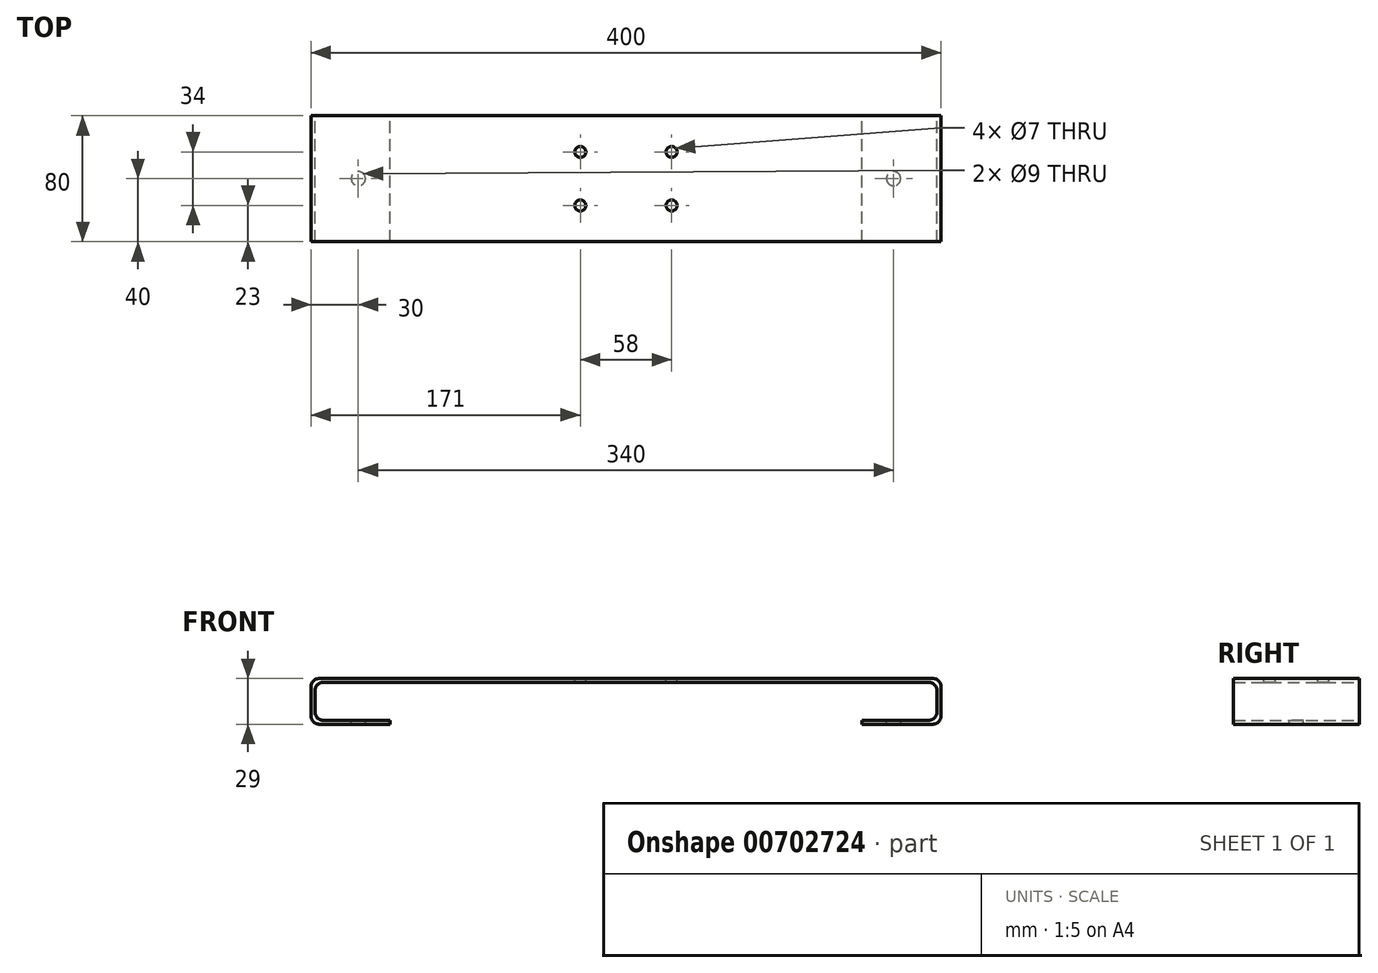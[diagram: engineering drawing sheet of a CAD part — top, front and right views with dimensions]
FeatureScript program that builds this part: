
annotation { "Feature Type Name" : "Feature", "Feature Type Description" : "" }
export const myFeature = defineFeature(function(context is Context, id is Id, definition is map)
    precondition{}
    {
        {
            var Q0;
            Q0=qCreatedBy(makeId("Front.planeOp"),FACE);
            var sketch = newSketch(context, id + "F0", { "sketchPlane" : qUnion([Q0])});
            skLineSegment(sketch, "E0", {"start": v(0, 0) * mm, "end": v(50, 0) * mm});
            skLineSegment(sketch, "E1", {"start": v(0, 0) * mm, "end": v(0, 29) * mm});
            skLineSegment(sketch, "E2", {"start": v(0, 29) * mm, "end": v(400, 29) * mm});
            skLineSegment(sketch, "E3", {"start": v(400, 29) * mm, "end": v(400, 0) * mm});
            skLineSegment(sketch, "E4", {"start": v(400, 0) * mm, "end": v(350, 0) * mm});
            skLineSegment(sketch, "E5.0", {"start": v(2.5, 2.5) * mm, "end": v(50, 2.5) * mm});
            skLineSegment(sketch, "E5.1", {"start": v(397.5, 2.5) * mm, "end": v(350, 2.5) * mm});
            skLineSegment(sketch, "E5.2", {"start": v(397.5, 26.5) * mm, "end": v(397.5, 2.5) * mm});
            skLineSegment(sketch, "E5.3", {"start": v(2.5, 26.5) * mm, "end": v(397.5, 26.5) * mm});
            skLineSegment(sketch, "E5.4", {"start": v(2.5, 2.5) * mm, "end": v(2.5, 26.5) * mm});
            skLineSegment(sketch, "E6", {"start": v(50, 2.5) * mm, "end": v(50, 0) * mm});
            skLineSegment(sketch, "E7", {"start": v(350, 2.5) * mm, "end": v(350, 0) * mm});
            skSolve(sketch);
        }
        {
            var Q0;
            Q0=qSketchRegion(id+"F0",true);
            extrude(context, id + "F1", {"entities" : qUnion([Q0]), "endBound" : BoundingType.SYMMETRIC, "depth" : 80 * mm, "offsetDistance" : 25 * mm});
        }
        {
            var Q0;
            Q0=makeQuery(id+"F1.opExtrude","SWEPT_FACE",FACE,{"disambiguationData":[OSD([sQuery(id+"F0.wireOp",EDGE,"E5.0")])]});
            var sketch = newSketch(context, id + "F2", { "sketchPlane" : qUnion([Q0])});
            skLineSegment(sketch, "E8", {"start": v(50, 0) * mm, "end": v(30, 0) * mm});
            skSolve(sketch);
        }
        {
            var Q0;
            Q0=makeQuery(id+"F1.opExtrude","SWEPT_FACE",FACE,{"disambiguationData":[OSD([sQuery(id+"F0.wireOp",EDGE,"E5.1")])]});
            var sketch = newSketch(context, id + "F3", { "sketchPlane" : qUnion([Q0])});
            skLineSegment(sketch, "E9", {"start": v(350, 0) * mm, "end": v(370, 0) * mm});
            skSolve(sketch);
        }
        {
            var Q0;
            Q0=sQuery(id+"F3.wireOp",VERTEX,"E9.end");
            var Q1;
            Q1=makeQuery(id+"F1.opExtrude","SWEPT_BODY",BODY,{"disambiguationData":[OSD([sQuery(id+"F0.wireOp",EDGE,"E0"),sQuery(id+"F0.wireOp",EDGE,"E1"),sQuery(id+"F0.wireOp",EDGE,"E2"),sQuery(id+"F0.wireOp",EDGE,"E3"),sQuery(id+"F0.wireOp",EDGE,"E4"),sQuery(id+"F0.wireOp",EDGE,"E5.0"),sQuery(id+"F0.wireOp",EDGE,"E5.1"),sQuery(id+"F0.wireOp",EDGE,"E5.2"),sQuery(id+"F0.wireOp",EDGE,"E5.3"),sQuery(id+"F0.wireOp",EDGE,"E5.4"),sQuery(id+"F0.wireOp",EDGE,"E6"),sQuery(id+"F0.wireOp",EDGE,"E7")])]});
            hole(context, id + "F4", {"style" : HoleStyle.SIMPLE, "endStyle" : HoleEndStyle.BLIND, "holeDiameter" : 9 * mm, "majorDiameter" : 5 * mm, "holeDepth" : 12 * mm, "isTappedThrough" : true, "tappedDepth" : 12 * mm, "tapClearance" : 3, "locations" : qUnion([Q0]), "scope" : qUnion([Q1])});
        }
        {
            var Q0;
            Q0=sQuery(id+"F2.wireOp",VERTEX,"E8.end");
            var Q1;
            Q1=makeQuery(id+"F1.opExtrude","SWEPT_BODY",BODY,{"disambiguationData":[OSD([sQuery(id+"F0.wireOp",EDGE,"E0"),sQuery(id+"F0.wireOp",EDGE,"E1"),sQuery(id+"F0.wireOp",EDGE,"E2"),sQuery(id+"F0.wireOp",EDGE,"E3"),sQuery(id+"F0.wireOp",EDGE,"E4"),sQuery(id+"F0.wireOp",EDGE,"E5.0"),sQuery(id+"F0.wireOp",EDGE,"E5.1"),sQuery(id+"F0.wireOp",EDGE,"E5.2"),sQuery(id+"F0.wireOp",EDGE,"E5.3"),sQuery(id+"F0.wireOp",EDGE,"E5.4"),sQuery(id+"F0.wireOp",EDGE,"E6"),sQuery(id+"F0.wireOp",EDGE,"E7")])]});
            hole(context, id + "F5", {"style" : HoleStyle.SIMPLE, "endStyle" : HoleEndStyle.BLIND, "holeDiameter" : 9 * mm, "majorDiameter" : 5 * mm, "holeDepth" : 12 * mm, "isTappedThrough" : true, "tappedDepth" : 12 * mm, "tapClearance" : 3, "locations" : qUnion([Q0]), "scope" : qUnion([Q1])});
        }
        {
            var Q0;
            Q0=makeQuery(id+"F1.opExtrude","SWEPT_FACE",FACE,{"disambiguationData":[OSD([sQuery(id+"F0.wireOp",EDGE,"E2")])]});
            var sketch = newSketch(context, id + "F6", { "sketchPlane" : qUnion([Q0])});
            skLineSegment(sketch, "E10", {"start": v(200, 40) * mm, "end": v(200, -40) * mm, "construction": true});
            skLineSegment(sketch, "E11", {"start": v(0, 0) * mm, "end": v(200, 0) * mm});
            skLineSegment(sketch, "E12.bottom", {"start": v(171, 17) * mm, "end": v(229, 17) * mm});
            skLineSegment(sketch, "E12.top", {"start": v(171, -17) * mm, "end": v(229, -17) * mm});
            skLineSegment(sketch, "E12.left", {"start": v(171, 17) * mm, "end": v(171, -17) * mm});
            skLineSegment(sketch, "E12.right", {"start": v(229, 17) * mm, "end": v(229, -17) * mm});
            skPoint(sketch, "E12.middle", {"position": v(200, 0) * mm});
            skSolve(sketch);
        }
        {
            var Q0;
            Q0=sQuery(id+"F6.wireOp",VERTEX,"E12.left.start");
            var Q1;
            Q1=sQuery(id+"F6.wireOp",VERTEX,"E12.right.start");
            var Q2;
            Q2=sQuery(id+"F6.wireOp",VERTEX,"E12.top.end");
            var Q3;
            Q3=sQuery(id+"F6.wireOp",VERTEX,"E12.left.end");
            var Q4;
            Q4=makeQuery(id+"F1.opExtrude","SWEPT_BODY",BODY,{"disambiguationData":[OSD([sQuery(id+"F0.wireOp",EDGE,"E0"),sQuery(id+"F0.wireOp",EDGE,"E1"),sQuery(id+"F0.wireOp",EDGE,"E2"),sQuery(id+"F0.wireOp",EDGE,"E3"),sQuery(id+"F0.wireOp",EDGE,"E4"),sQuery(id+"F0.wireOp",EDGE,"E5.0"),sQuery(id+"F0.wireOp",EDGE,"E5.1"),sQuery(id+"F0.wireOp",EDGE,"E5.2"),sQuery(id+"F0.wireOp",EDGE,"E5.3"),sQuery(id+"F0.wireOp",EDGE,"E5.4"),sQuery(id+"F0.wireOp",EDGE,"E6"),sQuery(id+"F0.wireOp",EDGE,"E7")])]});
            hole(context, id + "F7", {"style" : HoleStyle.SIMPLE, "endStyle" : HoleEndStyle.THROUGH, "holeDiameter" : 7 * mm, "majorDiameter" : 5 * mm, "isTappedThrough" : true, "tappedDepth" : 12 * mm, "tapClearance" : 3, "locations" : qUnion([Q0, Q1, Q2, Q3]), "scope" : qUnion([Q4])});
        }
        {
            var Q0;
            Q0=makeQuery(id+"F1.opExtrude","SWEPT_EDGE",EDGE,{"disambiguationData":[OSD([sQuery(id+"F0.wireOp",EDGE,"E1"),sQuery(id+"F0.wireOp",EDGE,"E2")])]});
            var Q1;
            Q1=makeQuery(id+"F1.opExtrude","SWEPT_EDGE",EDGE,{"disambiguationData":[OSD([sQuery(id+"F0.wireOp",EDGE,"E0"),sQuery(id+"F0.wireOp",EDGE,"E1")])]});
            var Q2;
            Q2=makeQuery(id+"F1.opExtrude","SWEPT_EDGE",EDGE,{"disambiguationData":[OSD([sQuery(id+"F0.wireOp",EDGE,"E2"),sQuery(id+"F0.wireOp",EDGE,"E3")])]});
            var Q3;
            Q3=makeQuery(id+"F1.opExtrude","SWEPT_EDGE",EDGE,{"disambiguationData":[OSD([sQuery(id+"F0.wireOp",EDGE,"E3"),sQuery(id+"F0.wireOp",EDGE,"E4")])]});
            var Q4;
            Q4=makeQuery(id+"F1.opExtrude","SWEPT_EDGE",EDGE,{"disambiguationData":[OSD([sQuery(id+"F0.wireOp",EDGE,"E5.0"),sQuery(id+"F0.wireOp",EDGE,"E5.4")])]});
            var Q5;
            Q5=makeQuery(id+"F1.opExtrude","SWEPT_EDGE",EDGE,{"disambiguationData":[OSD([sQuery(id+"F0.wireOp",EDGE,"E5.3"),sQuery(id+"F0.wireOp",EDGE,"E5.4")])]});
            var Q6;
            Q6=makeQuery(id+"F1.opExtrude","SWEPT_EDGE",EDGE,{"disambiguationData":[OSD([sQuery(id+"F0.wireOp",EDGE,"E5.1"),sQuery(id+"F0.wireOp",EDGE,"E5.2")])]});
            var Q7;
            Q7=makeQuery(id+"F1.opExtrude","SWEPT_EDGE",EDGE,{"disambiguationData":[OSD([sQuery(id+"F0.wireOp",EDGE,"E5.2"),sQuery(id+"F0.wireOp",EDGE,"E5.3")])]});
            fillet(context, id + "F8", {"entities" : qUnion([Q0, Q1, Q2, Q3, Q4, Q5, Q6, Q7]), "radius" : 5 * mm, "tangentPropagation" : true, "allowEdgeOverflow" : false});
        }
    });
